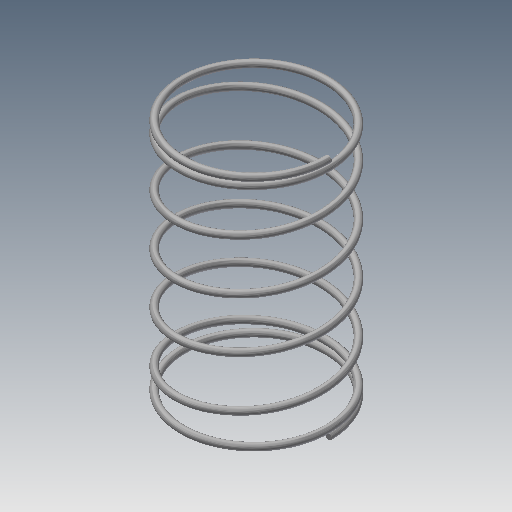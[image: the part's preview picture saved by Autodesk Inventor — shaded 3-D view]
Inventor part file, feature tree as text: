
AUTODESK INVENTOR PART (.ipt)
format: ipt  version: 2018.1 (Build 221171000, 171)  size: 732,672 bytes
history: native  units: mm
features: other x69, extrude x8, sketch x4, helix x3, sweep x2
ambient origin geometry x8: Origin, YZ Plane, XZ Plane, XY Plane, X Axis, Y Axis, Z Axis, Center Point
bodies: Solid1 (feature_tree)
feature tree (86):
  other  "Траектория основной пружины (справа)"
  other  "Рабочая плоскость сечения (справа)"
  other  "Начальная рабочая плоскость (справа)"
  other  "Конечная рабочая плоскость (справа)"
  other  "Рабочая плоскость конечного разреза (справа)"
  other  "Рабочая плоскость начального разреза (справа)"
  other  "Рабочая плоскость разреза торца 1 (справа)"
  other  "Рабочая плоскость разреза торца 2 (справа)"
  sweep  "Main Coil Feature(R)"
  other  "Поджатый виток в начале пружины 1 (справа)"
  helix  "Coil  Start Transition 2(R)"  [1 undecoded]
  helix  "Coil  Start Transition 3(R)"  [1 undecoded]
  helix  "Coil  Start Transition 4(R)"  [1 undecoded]
  other  "Торцевой виток в начале пружины (справа)"
  extrude  "Начальный разрез (справа)"  Depth=10.0mm
  other  "Поджатый виток в конце пружины 1 (справа)"
  other  "Поджатый виток в конце пружины 2 (справа)"
  other  "Поджатый виток в конце пружины 3 (справа)"
  other  "Поджатый виток в конце пружины 4 (справа)"
  other  "Торцевой виток (справа)"
  extrude  "Конечный разрез (справа)"  Depth=10.0mm
  extrude  "Разрез торца 1(справа)"  Depth=10.0mm
  extrude  "Plain Ends Cut  2(R)"  Depth=10.0mm TaperAngle=0.0deg
  other  "Траектория главной пружины (слева)"
  other  "Рабочая плоскость сечения (слева)"
  other  "Начальная рабочая плоскость (слева)"
  other  "Конечная рабочая плоскость (слева)"
  other  "Рабочая плоскость конечного разреза (слева)"
  other  "Рабочая плоскость начального разреза (слева)"
  other  "Рабочая плоскость разреза торца 1 (слева)"
  other  "Рабочая плоскость разреза торца 2 (слева)"
  sweep  "Main Coil Feature(L)"
  other  "Поджатый виток в начале пружины 1 (слева)"
  other  "Поджатый виток в начале пружины 2 (слева)"
  other  "Поджатый виток в начале пружины 3 (слева)"
  other  "Поджатый виток в начале пружины 4 (слева)"
  other  "Торцевой виток в начале пружины (слева)"
  extrude  "Начальный разрез (слева)"  Depth=10.0mm TaperAngle=0.0deg
  other  "Поджатый виток в конце пружины 1 (слева)"
  other  "Поджатый виток в конце пружины 2 (слева)"
  other  "Поджатый виток в конце пружины 3 (слева)"
  other  "Поджатый виток в конце пружины 4 (слева)"
  other  "Торцевой виток (слева)"
  extrude  "Конечный разрез (слева)"  [1 undecoded]
  extrude  "Cut Plain Ends Cut 1(L)"  Depth=10.0mm
  extrude  "Cut Plain Ends Cut 2(L)"  TaperAngle=0.0deg  [1 undecoded]
  other  "Рабочая плоскость конструктивной пары"
  other  "Просмотр центра"
  other  "Просмотр оси X"
  other  "Эскиз сегмента траектории (справа)"
  other  "Srf1"
  other  "Эскиз участка пружины (справа)"
  other  "Эскиз поджатого витка в начале пружины 1 (справа)"
  sketch  "Sketch  Start Transition 2(R)"  dims[d0=0.125mm d2=3.689815mm d3=10.0mm d4=40.0mm]
  sketch  "Sketch  Start Transition 3(R)"  dims[d5=0.0mm d6=90.0deg d7=90.0deg d8=0.0mm d9=0.0mm d12=1.599659mm d13=-1.599659mm d14=0.5mm]
  sketch  "Sketch  Start Transition 4(R)"  dims[d15=0.0mm]
  other  "Эскиз поджатого витка в конце пружины 1 (справа)"
  other  "Эскиз поджатого витка в конце пружины 2 (справа)"
  other  "Эскиз поджатого витка в конце пружины 3 (справа)"
  other  "Эскиз поджатого витка в конце пружины 4 (справа)"
  other  "Эскиз торца в начале пружины (справа)"
  other  "Эскиз торцевого витка (справа)"
  other  "Эскиз конечного разреза (справа)"
  other  "Эскиз начального разреза (справа)"
  other  "Эскиз сегмента траектории (слева)"
  other  "Srf2"
  other  "Эскиз участка пружины (слева)"
  other  "Эскиз поджатого витка в начале пружины 1 (слева)"
  other  "Эскиз поджатого витка в начале пружины 2 (слева)"
  other  "Эскиз поджатого витка в начале пружины 3 (слева)"
  sketch  "Sketch Start Transition 4(L)"  dims[d16=2.892361mm d17=10.0mm d18=1.25mm d19=0.0mm d20=90.0deg d21=90.0deg d22=0.0mm d23=0.0mm d24=2.094908mm d25=10.0mm d26=1.25mm d27=0.0mm d28=90.0deg d29=90.0deg d30=0.0mm d31=0.0mm d32=1.297454mm d33=10.0mm d34=1.25mm d35=0.0mm d36=90.0deg d37=90.0deg d38=0.0mm d39=0.0mm d40=0.5mm d41=10.0mm d42=1.25mm d43=0.0mm d44=90.0deg d45=90.0deg d46=0.0mm d47=0.0mm d48=2.892361mm d49=10.0mm d50=1.25mm d51=0.0mm d52=90.0deg d53=90.0deg d54=0.0mm d55=0.0mm d56=2.094908mm d57=10.0mm d58=1.25mm d59=0.0mm d60=90.0deg d61=90.0deg d62=0.0mm d63=0.0mm d64=1.297454mm d65=10.0mm d66=1.25mm d67=0.0mm d68=90.0deg d69=90.0deg d70=0.0mm d71=0.0mm d72=0.5mm d73=10.0mm d74=1.25mm d75=0.0mm d76=90.0deg d77=90.0deg d78=0.0mm d79=0.0mm d81=10.0mm d82=10.0mm d83=0.0mm d84=90.0deg d85=90.0deg d86=0.0mm d87=0.0mm d88=0.503118mm d89=10.0mm d90=10.0mm d91=0.0mm d92=90.0deg d93=90.0deg d94=0.0mm d95=0.0mm d96=11.0mm d97=0.503118mm d98=0.0mm d99=11.0mm d100=0.503118mm d101=0.0mm d102=0.0mm d103=0.0mm d104=0.0mm d105=0.0mm d106=0.0mm d108=0.0mm d112=0.0mm d113=10.0mm d114=0.0mm d121=-0.248451mm d131=10.0mm d132=0.0mm d133=0.0mm d134=0.0mm d135=0.125mm d137=3.689815mm d138=10.0mm d139=40.0mm d140=0.0mm d141=90.0deg d142=90.0deg d143=0.0mm d144=0.0mm d145=1.599659mm d146=-1.599659mm d147=-0.248451mm d148=-0.248451mm d149=0.5mm d150=0.0mm d151=0.0mm d152=2.892361mm d153=10.0mm d154=1.25mm d155=0.0mm d156=90.0deg d157=90.0deg d158=0.0mm d159=0.0mm d160=2.094908mm d161=10.0mm d162=1.25mm d163=0.0mm d164=90.0deg d165=90.0deg d166=0.0mm d167=0.0mm d168=1.297454mm d169=10.0mm d170=1.25mm d171=0.0mm d172=90.0deg d173=90.0deg d174=0.0mm d175=0.0mm d176=0.5mm d177=10.0mm d178=1.25mm d179=0.0mm d180=90.0deg d181=90.0deg d182=0.0mm d183=0.0mm d184=10.0mm d185=10.0mm d186=10.0mm d187=10.0mm d188=0.503118mm d189=10.0mm d190=10.0mm d191=0.0mm d192=90.0deg d193=90.0deg d194=0.0mm d195=0.0mm d196=10.0mm d197=11.0mm d198=0.503118mm d199=0.0mm d200=20.0mm d201=2.892361mm d202=10.0mm d203=1.25mm d204=0.0mm d205=90.0deg d206=90.0deg d207=0.0mm d208=0.0mm d209=10.0mm d210=2.094908mm d211=10.0mm d212=1.25mm d213=0.0mm d214=90.0deg d215=90.0deg d216=0.0mm d217=0.0mm d218=1.297454mm d219=10.0mm d220=1.25mm d221=0.0mm d222=90.0deg d223=90.0deg d224=0.0mm d225=0.0mm d226=0.5mm d227=10.0mm d228=1.25mm d229=0.0mm d230=90.0deg d231=90.0deg d232=0.0mm d233=0.0mm d234=10.0mm d235=10.0mm d236=10.0mm d237=0.503118mm d238=10.0mm d239=10.0mm d240=0.0mm d241=90.0deg d242=90.0deg d243=0.0mm d244=0.0mm d245=11.0mm d246=0.503118mm d247=0.0mm d248=10.0mm d249=20.0mm d254=11.0mm d255=10.0mm d256=0.0mm d257=30.0mm d258=0.248451mm d259=11.0mm d260=10.0mm d261=0.0mm d262=20.0mm d263=11.0mm d264=10.0mm d265=0.0mm d266=20.0mm d267=0.0mm d270=-1.537159mm d271=0.0mm d272=11.0mm d273=10.0mm d274=0.0mm d275=30.0mm d276=-94.24778mm d277=10.5mm d278=10.5mm d279=0.0mm d280=0.0mm]
  other  "Эскиз торца в начале пружины (слева)"
  other  "Эскиз начального разреза (слева)"
  other  "Эскиз поджатого витка в конце пружины 1 (слева)"
  other  "Эскиз поджатого витка в конце пружины 2 (слева)"
  other  "Эскиз поджатого витка в конце пружины 3 (слева)"
  other  "Эскиз поджатого витка в конце пружины 4 (слева)"
  other  "Эскиз торцевого витка (слева)"
  other  "Эскиз конечного разреза (слева)"
  other  "Эскиз разреза торца 2 (слева)"
  other  "Эскиз разреза торца 2 (справа)"
  other  "Эскиз разреза торца 1 (справа)"
  other  "Эскиз разреза торца 1 (слева)"
  other  "Начало линии разреза рабочей плоскости"
  other  "Базовая кривая (справа)"
  other  "Базовая кривая (слева)"
note: 5 required parameter values undecoded (feature->parameter linkage not recoverable at this tier; creation-order binding heuristic only, values carry confidence <= 0.55)
